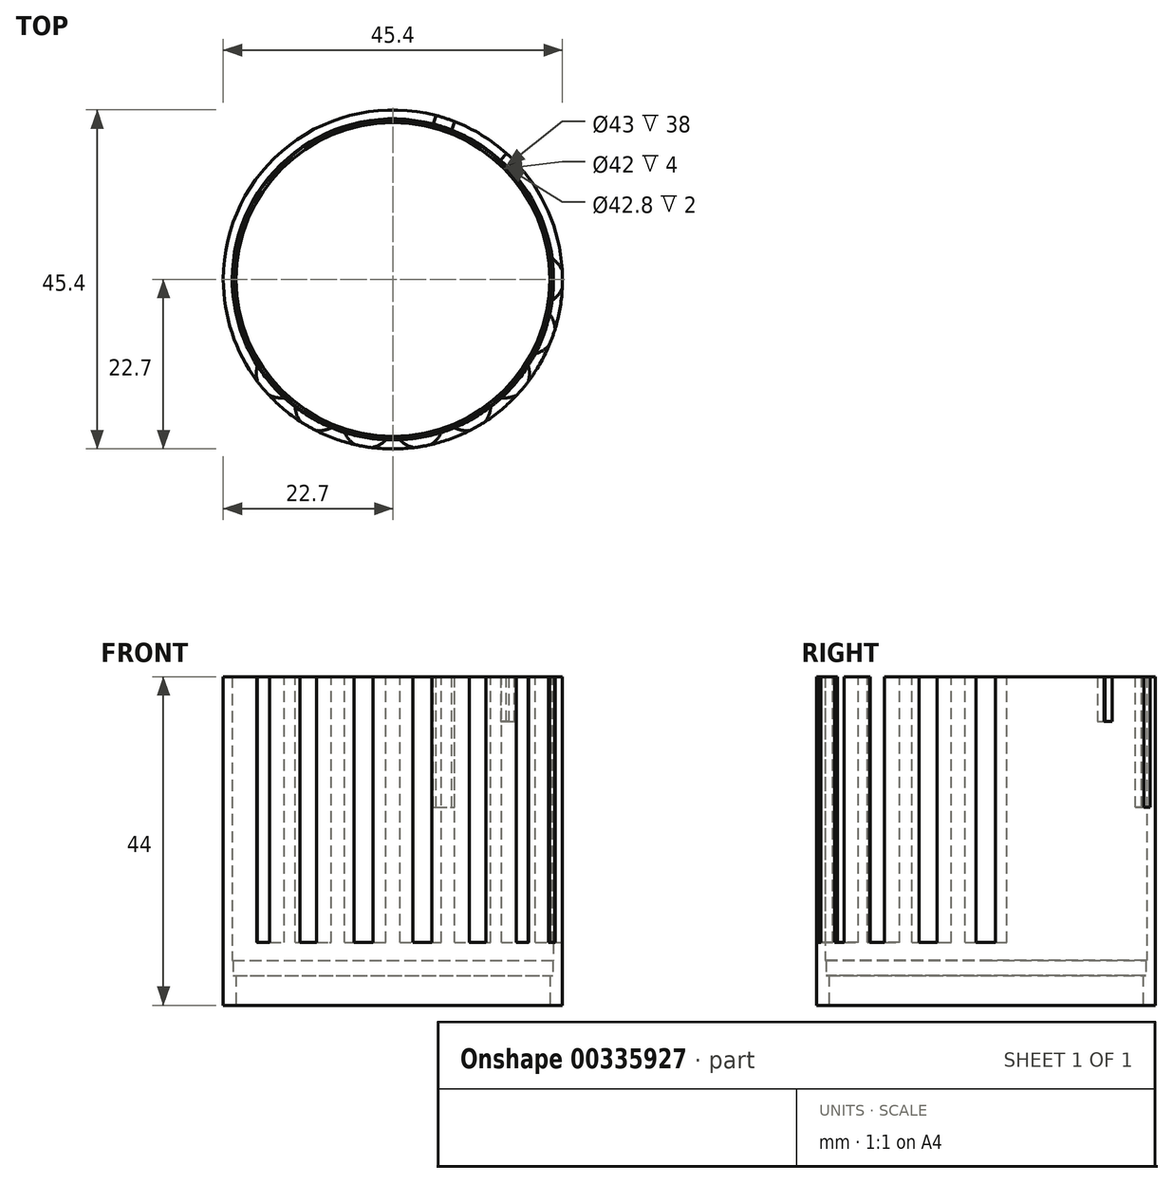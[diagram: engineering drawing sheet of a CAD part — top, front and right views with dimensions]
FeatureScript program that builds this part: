
annotation { "Feature Type Name" : "Feature", "Feature Type Description" : "" }
export const myFeature = defineFeature(function(context is Context, id is Id, definition is map)
    precondition{}
    {
        {
            var Q0;
            Q0=qCreatedBy(makeId("Front.planeOp"),FACE);
            var sketch = newSketch(context, id + "F0", { "sketchPlane" : qUnion([Q0])});
            skLineSegment(sketch, "E0", {"start": v(-22.7, 0) * mm, "end": v(-22.7, 44) * mm});
            skLineSegment(sketch, "E1", {"start": v(-22.7, 44) * mm, "end": v(-21.5, 44) * mm});
            skLineSegment(sketch, "E2", {"start": v(-21.5, 44) * mm, "end": v(-21.5, 6) * mm});
            skLineSegment(sketch, "E3", {"start": v(-21.5, 6) * mm, "end": v(-21.4, 6) * mm});
            skLineSegment(sketch, "E4", {"start": v(-21.4, 6) * mm, "end": v(-21.4, 4) * mm});
            skLineSegment(sketch, "E5", {"start": v(-21.4, 4) * mm, "end": v(-21, 4) * mm});
            skLineSegment(sketch, "E6", {"start": v(-21, 4) * mm, "end": v(-21, 0) * mm});
            skLineSegment(sketch, "E7", {"start": v(-21, 0) * mm, "end": v(-22.7, 0) * mm});
            skLineSegment(sketch, "E8", {"start": v(0, 0) * mm, "end": v(0, 44) * mm, "construction": true});
            skSolve(sketch);
        }
        {
            var Q0;
            Q0 = qSketchRegion(id + "F0", true);
            var Q1;
            Q1=sQuery(id+"F0.wireOp",EDGE,"E8");
            revolve(context, id + "F1", {"entities" : qUnion([Q0]), "axis" : qUnion([Q1]), "revolveType" : RevolveType.FULL});
        }
        {
            var Q0;
            Q0=makeQuery(id+"F1.opRevolve","SWEPT_FACE",FACE,{"disambiguationData":[OSD([sQuery(id+"F0.wireOp",EDGE,"E1")])]});
            var sketch = newSketch(context, id + "F2", { "sketchPlane" : qUnion([Q0])});
            skCircle(sketch, "E9", {"center": v(0, 0) * mm, "radius": 19.57 * mm, "construction": true});
            skLineSegment(sketch, "E10", {"start": v(0, 0) * mm, "end": v(6.05, 18.6) * mm, "construction": true});
            skLineSegment(sketch, "E11", {"start": v(12.58, 14.99) * mm, "end": v(0, 0) * mm, "construction": true});
            skLineSegment(sketch, "E12", {"start": v(19.57, 0) * mm, "end": v(0, 0) * mm, "construction": true});
            skLineSegment(sketch, "E13", {"start": v(18.39, -6.7) * mm, "end": v(0, 0) * mm, "construction": true});
            skLineSegment(sketch, "E14", {"start": v(14.99, -12.58) * mm, "end": v(0, 0) * mm, "construction": true});
            skLineSegment(sketch, "E15", {"start": v(9.78, -16.95) * mm, "end": v(0, 0) * mm, "construction": true});
            skLineSegment(sketch, "E16", {"start": v(3.4, -19.27) * mm, "end": v(0, 0) * mm, "construction": true});
            skLineSegment(sketch, "E17", {"start": v(-3.4, -19.27) * mm, "end": v(0, 0) * mm, "construction": true});
            skLineSegment(sketch, "E18", {"start": v(-9.78, -16.95) * mm, "end": v(0, 0) * mm, "construction": true});
            skCircle(sketch, "E19", {"center": v(19.57, 0) * mm, "radius": 3.3 * mm});
            skCircle(sketch, "E20", {"center": v(18.39, -6.7) * mm, "radius": 3.3 * mm});
            skCircle(sketch, "E21", {"center": v(14.99, -12.58) * mm, "radius": 3.3 * mm});
            skCircle(sketch, "E22", {"center": v(9.78, -16.95) * mm, "radius": 3.3 * mm});
            skCircle(sketch, "E23", {"center": v(3.4, -19.27) * mm, "radius": 3.3 * mm});
            skCircle(sketch, "E24", {"center": v(-3.4, -19.27) * mm, "radius": 3.3 * mm});
            skCircle(sketch, "E25", {"center": v(-9.78, -16.95) * mm, "radius": 3.3 * mm});
            skLineSegment(sketch, "E26", {"start": v(0, 0) * mm, "end": v(-14.99, -12.58) * mm, "construction": true});
            skCircle(sketch, "E27", {"center": v(-14.99, -12.58) * mm, "radius": 3.3 * mm});
            skCircle(sketch, "E28.0", {"center": v(0, 0) * mm, "radius": 21 * mm, "construction": true});
            skCircle(sketch, "E29.0", {"center": v(0, 0) * mm, "radius": 22.7 * mm, "construction": true});
            skLineSegment(sketch, "E30", {"start": v(20.96, 1.3) * mm, "end": v(22.66, 1.3) * mm});
            skLineSegment(sketch, "E31.MirrorCS", {"start": v(20.96, -1.3) * mm, "end": v(22.66, -1.3) * mm});
            skLineSegment(sketch, "E32", {"start": v(20.14, -5.95) * mm, "end": v(21.74, -6.53) * mm});
            skLineSegment(sketch, "E33.MirrorCS", {"start": v(19.25, -8.4) * mm, "end": v(20.85, -8.97) * mm});
            skLineSegment(sketch, "E34", {"start": v(15.8, -11.55) * mm, "end": v(18.2, -13.57) * mm});
            skLineSegment(sketch, "E35.MirrorCS", {"start": v(14.12, -13.55) * mm, "end": v(16.53, -15.56) * mm});
            skLineSegment(sketch, "E36", {"start": v(11.6, -17.5) * mm, "end": v(12.46, -18.98) * mm});
            skLineSegment(sketch, "E37.MirrorCS", {"start": v(9.35, -18.8) * mm, "end": v(10.2, -20.28) * mm});
            skLineSegment(sketch, "E38", {"start": v(4.92, -20.42) * mm, "end": v(5.22, -22.1) * mm});
            skLineSegment(sketch, "E39", {"start": v(-2.36, -20.87) * mm, "end": v(-2.66, -22.54) * mm});
            skLineSegment(sketch, "E40", {"start": v(-9.35, -18.8) * mm, "end": v(-10.2, -20.28) * mm});
            skLineSegment(sketch, "E41", {"start": v(-15.22, -14.47) * mm, "end": v(-16.53, -15.56) * mm});
            skLineSegment(sketch, "E42.MirrorCS", {"start": v(2.36, -20.87) * mm, "end": v(2.66, -22.54) * mm});
            skLineSegment(sketch, "E43.MirrorCS", {"start": v(-4.92, -20.42) * mm, "end": v(-5.22, -22.1) * mm});
            skLineSegment(sketch, "E44.MirrorCS", {"start": v(-11.6, -17.5) * mm, "end": v(-12.46, -18.98) * mm});
            skLineSegment(sketch, "E45.MirrorCS", {"start": v(-16.9, -12.48) * mm, "end": v(-18.2, -13.57) * mm});
            skLineSegment(sketch, "E46", {"start": v(5.24, 20.34) * mm, "end": v(5.77, 21.96) * mm});
            skLineSegment(sketch, "E47.MirrorCS", {"start": v(7.71, 19.53) * mm, "end": v(8.24, 21.15) * mm});
            skArc(sketch, "E48", {"start": v(5.24, 20.34) * mm, "mid": v(6.49, 19.97) * mm, "end": v(7.71, 19.53) * mm});
            skArc(sketch, "E49", {"start": v(5.77, 21.96) * mm, "mid": v(7.01, 21.59) * mm, "end": v(8.24, 21.15) * mm});
            skLineSegment(sketch, "E50", {"start": v(14.1, 15.56) * mm, "end": v(15.2, 16.86) * mm});
            skLineSegment(sketch, "E51", {"start": v(15.18, 14.51) * mm, "end": v(16.28, 15.82) * mm});
            skArc(sketch, "E52", {"start": v(15.18, 14.51) * mm, "mid": v(14.65, 15.05) * mm, "end": v(14.1, 15.56) * mm});
            skArc(sketch, "E53", {"start": v(16.28, 15.82) * mm, "mid": v(15.75, 16.35) * mm, "end": v(15.2, 16.86) * mm});
            skSolve(sketch);
        }
        {
            var Q0;
            {var subQ0=sQuery(id+"F2.wireOp",EDGE,"E30");var subQ1=sQuery(id+"F2.wireOp",EDGE,"E19");var subQ2=makeQuery(id+"F2.imprint","INTERSECT",VERTEX,{"derivedFrom":[subQ1,subQ0]});Q0=makeQuery(id+"F2.imprint","IMPRINT",FACE,{"disambiguationData":[TD([[makeQuery(id+"F2.imprint","IMPRINT",EDGE,{"disambiguationData":[TD([[subQ2,1.0]])],"derivedFrom":subQ1}),1.0]])]});}
            var Q1;
            {var subQ0=sQuery(id+"F2.wireOp",EDGE,"E30");var subQ1=sQuery(id+"F2.wireOp",EDGE,"E19");var subQ2=makeQuery(id+"F2.imprint","INTERSECT",VERTEX,{"derivedFrom":[subQ1,subQ0]});Q1=makeQuery(id+"F2.imprint","IMPRINT",FACE,{"disambiguationData":[TD([[makeQuery(id+"F2.imprint","IMPRINT",EDGE,{"disambiguationData":[TD([[subQ2,-1.0]])],"derivedFrom":subQ1}),1.0]])]});}
            var Q2;
            {var subQ0=sQuery(id+"F2.wireOp",EDGE,"E30");var subQ1=sQuery(id+"F2.wireOp",EDGE,"E19");var subQ2=makeQuery(id+"F2.imprint","INTERSECT",VERTEX,{"derivedFrom":[subQ1,subQ0]});Q2=makeQuery(id+"F2.imprint","IMPRINT",FACE,{"disambiguationData":[TD([[makeQuery(id+"F2.imprint","IMPRINT",EDGE,{"disambiguationData":[TD([[subQ2,1.0]])],"derivedFrom":subQ1}),-1.0]])]});}
            var Q3;
            {var subQ0=sQuery(id+"F2.wireOp",EDGE,"E31.MirrorCS");var subQ1=sQuery(id+"F2.wireOp",EDGE,"E19");var subQ2=makeQuery(id+"F2.imprint","INTERSECT",VERTEX,{"derivedFrom":[subQ1,subQ0]});Q3=makeQuery(id+"F2.imprint","IMPRINT",FACE,{"disambiguationData":[TD([[makeQuery(id+"F2.imprint","IMPRINT",EDGE,{"disambiguationData":[TD([[subQ2,-1.0]])],"derivedFrom":subQ1}),-1.0]])]});}
            var Q4;
            {var subQ0=sQuery(id+"F2.wireOp",EDGE,"E31.MirrorCS");var subQ1=sQuery(id+"F2.wireOp",EDGE,"E19");var subQ2=makeQuery(id+"F2.imprint","INTERSECT",VERTEX,{"derivedFrom":[subQ1,subQ0]});Q4=makeQuery(id+"F2.imprint","IMPRINT",FACE,{"disambiguationData":[TD([[makeQuery(id+"F2.imprint","IMPRINT",EDGE,{"disambiguationData":[TD([[subQ2,1.0]])],"derivedFrom":subQ1}),1.0]])]});}
            var Q5;
            {var subQ0=sQuery(id+"F2.wireOp",EDGE,"E19");var subQ1=makeQuery(id+"F1.opRevolve","SWEPT_EDGE",EDGE,{"disambiguationData":[OSD([sQuery(id+"F0.wireOp",EDGE,"E1"),sQuery(id+"F0.wireOp",EDGE,"E2")])]});var subQ2=makeQuery(id+"F2.imprint","INTERSECT",VERTEX,{"disambiguationData":[OD(0.0)],"derivedFrom":[subQ1,subQ0]});Q5=makeQuery(id+"F2.imprint","IMPRINT",FACE,{"disambiguationData":[TD([[makeQuery(id+"F2.imprint","IMPRINT",EDGE,{"disambiguationData":[TD([[subQ2,-1.0]])],"derivedFrom":subQ0}),1.0]])]});}
            var Q6;
            {var subQ0=sQuery(id+"F2.wireOp",EDGE,"E20");var subQ1=makeQuery(id+"F1.opRevolve","SWEPT_EDGE",EDGE,{"disambiguationData":[OSD([sQuery(id+"F0.wireOp",EDGE,"E1"),sQuery(id+"F0.wireOp",EDGE,"E2")])]});var subQ2=makeQuery(id+"F2.imprint","INTERSECT",VERTEX,{"disambiguationData":[OD(0.0)],"derivedFrom":[subQ1,subQ0]});Q6=makeQuery(id+"F2.imprint","IMPRINT",FACE,{"disambiguationData":[TD([[makeQuery(id+"F2.imprint","IMPRINT",EDGE,{"disambiguationData":[TD([[subQ2,-1.0]])],"derivedFrom":subQ0}),1.0]])]});}
            var Q7;
            {var subQ0=sQuery(id+"F2.wireOp",EDGE,"E32");var subQ1=sQuery(id+"F2.wireOp",EDGE,"E20");var subQ2=makeQuery(id+"F2.imprint","INTERSECT",VERTEX,{"derivedFrom":[subQ1,subQ0]});Q7=makeQuery(id+"F2.imprint","IMPRINT",FACE,{"disambiguationData":[TD([[makeQuery(id+"F2.imprint","IMPRINT",EDGE,{"disambiguationData":[TD([[subQ2,-1.0]])],"derivedFrom":subQ1}),1.0]])]});}
            var Q8;
            {var subQ1=sQuery(id+"F2.wireOp",EDGE,"E20");var subQ8=sQuery(id+"F2.wireOp",EDGE,"E33.MirrorCS");var subQ9=makeQuery(id+"F2.imprint","INTERSECT",VERTEX,{"derivedFrom":[subQ1,subQ8]});Q8=makeQuery(id+"F2.imprint","IMPRINT",FACE,{"disambiguationData":[TD([[makeQuery(id+"F2.imprint","IMPRINT",EDGE,{"disambiguationData":[TD([[subQ9,-1.0]])],"derivedFrom":subQ1}),1.0]])]});}
            var Q9;
            {var subQ0=sQuery(id+"F2.wireOp",EDGE,"E33.MirrorCS");var subQ1=sQuery(id+"F2.wireOp",EDGE,"E20");var subQ2=makeQuery(id+"F2.imprint","INTERSECT",VERTEX,{"derivedFrom":[subQ1,subQ0]});Q9=makeQuery(id+"F2.imprint","IMPRINT",FACE,{"disambiguationData":[TD([[makeQuery(id+"F2.imprint","IMPRINT",EDGE,{"disambiguationData":[TD([[subQ2,1.0]])],"derivedFrom":subQ1}),1.0]])]});}
            var Q10;
            {var subQ0=sQuery(id+"F2.wireOp",EDGE,"E32");var subQ1=sQuery(id+"F2.wireOp",EDGE,"E20");var subQ2=makeQuery(id+"F2.imprint","INTERSECT",VERTEX,{"derivedFrom":[subQ1,subQ0]});Q10=makeQuery(id+"F2.imprint","IMPRINT",FACE,{"disambiguationData":[TD([[makeQuery(id+"F2.imprint","IMPRINT",EDGE,{"disambiguationData":[TD([[subQ2,1.0]])],"derivedFrom":subQ1}),-1.0]])]});}
            var Q11;
            {var subQ0=sQuery(id+"F2.wireOp",EDGE,"E33.MirrorCS");var subQ1=sQuery(id+"F2.wireOp",EDGE,"E20");var subQ2=makeQuery(id+"F2.imprint","INTERSECT",VERTEX,{"derivedFrom":[subQ1,subQ0]});Q11=makeQuery(id+"F2.imprint","IMPRINT",FACE,{"disambiguationData":[TD([[makeQuery(id+"F2.imprint","IMPRINT",EDGE,{"disambiguationData":[TD([[subQ2,-1.0]])],"derivedFrom":subQ1}),-1.0]])]});}
            var Q12;
            {var subQ0=sQuery(id+"F2.wireOp",EDGE,"E21");var subQ1=makeQuery(id+"F1.opRevolve","SWEPT_EDGE",EDGE,{"disambiguationData":[OSD([sQuery(id+"F0.wireOp",EDGE,"E1"),sQuery(id+"F0.wireOp",EDGE,"E2")])]});var subQ2=makeQuery(id+"F2.imprint","INTERSECT",VERTEX,{"disambiguationData":[OD(0.0)],"derivedFrom":[subQ1,subQ0]});Q12=makeQuery(id+"F2.imprint","IMPRINT",FACE,{"disambiguationData":[TD([[makeQuery(id+"F2.imprint","IMPRINT",EDGE,{"disambiguationData":[TD([[subQ2,1.0]])],"derivedFrom":subQ0}),1.0]])]});}
            var Q13;
            {var subQ0=sQuery(id+"F2.wireOp",EDGE,"E34");var subQ1=sQuery(id+"F2.wireOp",EDGE,"E21");var subQ2=makeQuery(id+"F2.imprint","INTERSECT",VERTEX,{"derivedFrom":[subQ1,subQ0]});Q13=makeQuery(id+"F2.imprint","IMPRINT",FACE,{"disambiguationData":[TD([[makeQuery(id+"F2.imprint","IMPRINT",EDGE,{"disambiguationData":[TD([[subQ2,-1.0]])],"derivedFrom":subQ1}),1.0]])]});}
            var Q14;
            {var subQ0=sQuery(id+"F2.wireOp",EDGE,"E35.MirrorCS");var subQ1=sQuery(id+"F2.wireOp",EDGE,"E21");var subQ2=makeQuery(id+"F2.imprint","INTERSECT",VERTEX,{"derivedFrom":[subQ1,subQ0]});Q14=makeQuery(id+"F2.imprint","IMPRINT",FACE,{"disambiguationData":[TD([[makeQuery(id+"F2.imprint","IMPRINT",EDGE,{"disambiguationData":[TD([[subQ2,-1.0]])],"derivedFrom":subQ1}),1.0]])]});}
            var Q15;
            {var subQ0=sQuery(id+"F2.wireOp",EDGE,"E35.MirrorCS");var subQ1=sQuery(id+"F2.wireOp",EDGE,"E21");var subQ2=makeQuery(id+"F2.imprint","INTERSECT",VERTEX,{"derivedFrom":[subQ1,subQ0]});Q15=makeQuery(id+"F2.imprint","IMPRINT",FACE,{"disambiguationData":[TD([[makeQuery(id+"F2.imprint","IMPRINT",EDGE,{"disambiguationData":[TD([[subQ2,1.0]])],"derivedFrom":subQ1}),1.0]])]});}
            var Q16;
            {var subQ0=sQuery(id+"F2.wireOp",EDGE,"E34");var subQ1=sQuery(id+"F2.wireOp",EDGE,"E21");var subQ2=makeQuery(id+"F2.imprint","INTERSECT",VERTEX,{"derivedFrom":[subQ1,subQ0]});Q16=makeQuery(id+"F2.imprint","IMPRINT",FACE,{"disambiguationData":[TD([[makeQuery(id+"F2.imprint","IMPRINT",EDGE,{"disambiguationData":[TD([[subQ2,1.0]])],"derivedFrom":subQ1}),-1.0]])]});}
            var Q17;
            {var subQ0=sQuery(id+"F2.wireOp",EDGE,"E35.MirrorCS");var subQ1=sQuery(id+"F2.wireOp",EDGE,"E21");var subQ2=makeQuery(id+"F2.imprint","INTERSECT",VERTEX,{"derivedFrom":[subQ1,subQ0]});Q17=makeQuery(id+"F2.imprint","IMPRINT",FACE,{"disambiguationData":[TD([[makeQuery(id+"F2.imprint","IMPRINT",EDGE,{"disambiguationData":[TD([[subQ2,-1.0]])],"derivedFrom":subQ1}),-1.0]])]});}
            var Q18;
            {var subQ0=sQuery(id+"F2.wireOp",EDGE,"E37.MirrorCS");var subQ1=sQuery(id+"F2.wireOp",EDGE,"E22");var subQ2=makeQuery(id+"F2.imprint","INTERSECT",VERTEX,{"derivedFrom":[subQ1,subQ0]});Q18=makeQuery(id+"F2.imprint","IMPRINT",FACE,{"disambiguationData":[TD([[makeQuery(id+"F2.imprint","IMPRINT",EDGE,{"disambiguationData":[TD([[subQ2,1.0]])],"derivedFrom":subQ1}),1.0]])]});}
            var Q19;
            {var subQ0=sQuery(id+"F2.wireOp",EDGE,"E37.MirrorCS");var subQ1=sQuery(id+"F2.wireOp",EDGE,"E22");var subQ2=makeQuery(id+"F2.imprint","INTERSECT",VERTEX,{"derivedFrom":[subQ1,subQ0]});Q19=makeQuery(id+"F2.imprint","IMPRINT",FACE,{"disambiguationData":[TD([[makeQuery(id+"F2.imprint","IMPRINT",EDGE,{"disambiguationData":[TD([[subQ2,-1.0]])],"derivedFrom":subQ1}),1.0]])]});}
            var Q20;
            {var subQ0=sQuery(id+"F2.wireOp",EDGE,"E36");var subQ1=sQuery(id+"F2.wireOp",EDGE,"E22");var subQ2=makeQuery(id+"F2.imprint","INTERSECT",VERTEX,{"derivedFrom":[subQ1,subQ0]});Q20=makeQuery(id+"F2.imprint","IMPRINT",FACE,{"disambiguationData":[TD([[makeQuery(id+"F2.imprint","IMPRINT",EDGE,{"disambiguationData":[TD([[subQ2,-1.0]])],"derivedFrom":subQ1}),1.0]])]});}
            var Q21;
            {var subQ0=sQuery(id+"F2.wireOp",EDGE,"E22");var subQ1=makeQuery(id+"F1.opRevolve","SWEPT_EDGE",EDGE,{"disambiguationData":[OSD([sQuery(id+"F0.wireOp",EDGE,"E1"),sQuery(id+"F0.wireOp",EDGE,"E2")])]});var subQ2=makeQuery(id+"F2.imprint","INTERSECT",VERTEX,{"disambiguationData":[OD(0.0)],"derivedFrom":[subQ1,subQ0]});Q21=makeQuery(id+"F2.imprint","IMPRINT",FACE,{"disambiguationData":[TD([[makeQuery(id+"F2.imprint","IMPRINT",EDGE,{"disambiguationData":[TD([[subQ2,1.0]])],"derivedFrom":subQ0}),1.0]])]});}
            var Q22;
            {var subQ0=sQuery(id+"F2.wireOp",EDGE,"E36");var subQ1=sQuery(id+"F2.wireOp",EDGE,"E22");var subQ2=makeQuery(id+"F2.imprint","INTERSECT",VERTEX,{"derivedFrom":[subQ1,subQ0]});Q22=makeQuery(id+"F2.imprint","IMPRINT",FACE,{"disambiguationData":[TD([[makeQuery(id+"F2.imprint","IMPRINT",EDGE,{"disambiguationData":[TD([[subQ2,1.0]])],"derivedFrom":subQ1}),-1.0]])]});}
            var Q23;
            {var subQ0=sQuery(id+"F2.wireOp",EDGE,"E37.MirrorCS");var subQ1=sQuery(id+"F2.wireOp",EDGE,"E22");var subQ2=makeQuery(id+"F2.imprint","INTERSECT",VERTEX,{"derivedFrom":[subQ1,subQ0]});Q23=makeQuery(id+"F2.imprint","IMPRINT",FACE,{"disambiguationData":[TD([[makeQuery(id+"F2.imprint","IMPRINT",EDGE,{"disambiguationData":[TD([[subQ2,-1.0]])],"derivedFrom":subQ1}),-1.0]])]});}
            var Q24;
            {var subQ0=sQuery(id+"F2.wireOp",EDGE,"E23");var subQ1=makeQuery(id+"F1.opRevolve","SWEPT_EDGE",EDGE,{"disambiguationData":[OSD([sQuery(id+"F0.wireOp",EDGE,"E1"),sQuery(id+"F0.wireOp",EDGE,"E2")])]});var subQ2=makeQuery(id+"F2.imprint","INTERSECT",VERTEX,{"disambiguationData":[OD(0.0)],"derivedFrom":[subQ1,subQ0]});Q24=makeQuery(id+"F2.imprint","IMPRINT",FACE,{"disambiguationData":[TD([[makeQuery(id+"F2.imprint","IMPRINT",EDGE,{"disambiguationData":[TD([[subQ2,1.0]])],"derivedFrom":subQ0}),1.0]])]});}
            var Q25;
            {var subQ0=sQuery(id+"F2.wireOp",EDGE,"E42.MirrorCS");var subQ1=sQuery(id+"F2.wireOp",EDGE,"E23");var subQ2=makeQuery(id+"F2.imprint","INTERSECT",VERTEX,{"derivedFrom":[subQ1,subQ0]});Q25=makeQuery(id+"F2.imprint","IMPRINT",FACE,{"disambiguationData":[TD([[makeQuery(id+"F2.imprint","IMPRINT",EDGE,{"disambiguationData":[TD([[subQ2,1.0]])],"derivedFrom":subQ1}),1.0]])]});}
            var Q26;
            {var subQ1=sQuery(id+"F2.wireOp",EDGE,"E23");var subQ9=sQuery(id+"F2.wireOp",EDGE,"E42.MirrorCS");var subQ10=makeQuery(id+"F2.imprint","INTERSECT",VERTEX,{"derivedFrom":[subQ1,subQ9]});Q26=makeQuery(id+"F2.imprint","IMPRINT",FACE,{"disambiguationData":[TD([[makeQuery(id+"F2.imprint","IMPRINT",EDGE,{"disambiguationData":[TD([[subQ10,-1.0]])],"derivedFrom":subQ1}),1.0]])]});}
            var Q27;
            {var subQ0=sQuery(id+"F2.wireOp",EDGE,"E38");var subQ1=sQuery(id+"F2.wireOp",EDGE,"E23");var subQ2=makeQuery(id+"F2.imprint","INTERSECT",VERTEX,{"derivedFrom":[subQ1,subQ0]});Q27=makeQuery(id+"F2.imprint","IMPRINT",FACE,{"disambiguationData":[TD([[makeQuery(id+"F2.imprint","IMPRINT",EDGE,{"disambiguationData":[TD([[subQ2,-1.0]])],"derivedFrom":subQ1}),1.0]])]});}
            var Q28;
            {var subQ0=sQuery(id+"F2.wireOp",EDGE,"E38");var subQ1=sQuery(id+"F2.wireOp",EDGE,"E23");var subQ2=makeQuery(id+"F2.imprint","INTERSECT",VERTEX,{"derivedFrom":[subQ1,subQ0]});Q28=makeQuery(id+"F2.imprint","IMPRINT",FACE,{"disambiguationData":[TD([[makeQuery(id+"F2.imprint","IMPRINT",EDGE,{"disambiguationData":[TD([[subQ2,1.0]])],"derivedFrom":subQ1}),-1.0]])]});}
            var Q29;
            {var subQ0=sQuery(id+"F2.wireOp",EDGE,"E42.MirrorCS");var subQ1=sQuery(id+"F2.wireOp",EDGE,"E23");var subQ2=makeQuery(id+"F2.imprint","INTERSECT",VERTEX,{"derivedFrom":[subQ1,subQ0]});Q29=makeQuery(id+"F2.imprint","IMPRINT",FACE,{"disambiguationData":[TD([[makeQuery(id+"F2.imprint","IMPRINT",EDGE,{"disambiguationData":[TD([[subQ2,-1.0]])],"derivedFrom":subQ1}),-1.0]])]});}
            var Q30;
            {var subQ0=sQuery(id+"F2.wireOp",EDGE,"E24");var subQ1=makeQuery(id+"F1.opRevolve","SWEPT_EDGE",EDGE,{"disambiguationData":[OSD([sQuery(id+"F0.wireOp",EDGE,"E1"),sQuery(id+"F0.wireOp",EDGE,"E2")])]});var subQ2=makeQuery(id+"F2.imprint","INTERSECT",VERTEX,{"disambiguationData":[OD(0.0)],"derivedFrom":[subQ1,subQ0]});Q30=makeQuery(id+"F2.imprint","IMPRINT",FACE,{"disambiguationData":[TD([[makeQuery(id+"F2.imprint","IMPRINT",EDGE,{"disambiguationData":[TD([[subQ2,1.0]])],"derivedFrom":subQ0}),1.0]])]});}
            var Q31;
            {var subQ0=sQuery(id+"F2.wireOp",EDGE,"E43.MirrorCS");var subQ1=sQuery(id+"F2.wireOp",EDGE,"E24");var subQ2=makeQuery(id+"F2.imprint","INTERSECT",VERTEX,{"derivedFrom":[subQ1,subQ0]});Q31=makeQuery(id+"F2.imprint","IMPRINT",FACE,{"disambiguationData":[TD([[makeQuery(id+"F2.imprint","IMPRINT",EDGE,{"disambiguationData":[TD([[subQ2,1.0]])],"derivedFrom":subQ1}),1.0]])]});}
            var Q32;
            {var subQ0=sQuery(id+"F2.wireOp",EDGE,"E43.MirrorCS");var subQ1=sQuery(id+"F2.wireOp",EDGE,"E24");var subQ2=makeQuery(id+"F2.imprint","INTERSECT",VERTEX,{"derivedFrom":[subQ1,subQ0]});Q32=makeQuery(id+"F2.imprint","IMPRINT",FACE,{"disambiguationData":[TD([[makeQuery(id+"F2.imprint","IMPRINT",EDGE,{"disambiguationData":[TD([[subQ2,-1.0]])],"derivedFrom":subQ1}),1.0]])]});}
            var Q33;
            {var subQ0=sQuery(id+"F2.wireOp",EDGE,"E39");var subQ1=sQuery(id+"F2.wireOp",EDGE,"E24");var subQ2=makeQuery(id+"F2.imprint","INTERSECT",VERTEX,{"derivedFrom":[subQ1,subQ0]});Q33=makeQuery(id+"F2.imprint","IMPRINT",FACE,{"disambiguationData":[TD([[makeQuery(id+"F2.imprint","IMPRINT",EDGE,{"disambiguationData":[TD([[subQ2,-1.0]])],"derivedFrom":subQ1}),1.0]])]});}
            var Q34;
            {var subQ0=sQuery(id+"F2.wireOp",EDGE,"E39");var subQ1=sQuery(id+"F2.wireOp",EDGE,"E24");var subQ2=makeQuery(id+"F2.imprint","INTERSECT",VERTEX,{"derivedFrom":[subQ1,subQ0]});Q34=makeQuery(id+"F2.imprint","IMPRINT",FACE,{"disambiguationData":[TD([[makeQuery(id+"F2.imprint","IMPRINT",EDGE,{"disambiguationData":[TD([[subQ2,1.0]])],"derivedFrom":subQ1}),-1.0]])]});}
            var Q35;
            {var subQ0=sQuery(id+"F2.wireOp",EDGE,"E43.MirrorCS");var subQ1=sQuery(id+"F2.wireOp",EDGE,"E24");var subQ2=makeQuery(id+"F2.imprint","INTERSECT",VERTEX,{"derivedFrom":[subQ1,subQ0]});Q35=makeQuery(id+"F2.imprint","IMPRINT",FACE,{"disambiguationData":[TD([[makeQuery(id+"F2.imprint","IMPRINT",EDGE,{"disambiguationData":[TD([[subQ2,-1.0]])],"derivedFrom":subQ1}),-1.0]])]});}
            var Q36;
            {var subQ0=sQuery(id+"F2.wireOp",EDGE,"E25");var subQ1=makeQuery(id+"F1.opRevolve","SWEPT_EDGE",EDGE,{"disambiguationData":[OSD([sQuery(id+"F0.wireOp",EDGE,"E1"),sQuery(id+"F0.wireOp",EDGE,"E2")])]});var subQ2=makeQuery(id+"F2.imprint","INTERSECT",VERTEX,{"disambiguationData":[OD(0.0)],"derivedFrom":[subQ1,subQ0]});Q36=makeQuery(id+"F2.imprint","IMPRINT",FACE,{"disambiguationData":[TD([[makeQuery(id+"F2.imprint","IMPRINT",EDGE,{"disambiguationData":[TD([[subQ2,1.0]])],"derivedFrom":subQ0}),1.0]])]});}
            var Q37;
            {var subQ0=sQuery(id+"F2.wireOp",EDGE,"E44.MirrorCS");var subQ1=sQuery(id+"F2.wireOp",EDGE,"E25");var subQ2=makeQuery(id+"F2.imprint","INTERSECT",VERTEX,{"derivedFrom":[subQ1,subQ0]});Q37=makeQuery(id+"F2.imprint","IMPRINT",FACE,{"disambiguationData":[TD([[makeQuery(id+"F2.imprint","IMPRINT",EDGE,{"disambiguationData":[TD([[subQ2,1.0]])],"derivedFrom":subQ1}),1.0]])]});}
            var Q38;
            {var subQ0=sQuery(id+"F2.wireOp",EDGE,"E44.MirrorCS");var subQ1=sQuery(id+"F2.wireOp",EDGE,"E25");var subQ2=makeQuery(id+"F2.imprint","INTERSECT",VERTEX,{"derivedFrom":[subQ1,subQ0]});Q38=makeQuery(id+"F2.imprint","IMPRINT",FACE,{"disambiguationData":[TD([[makeQuery(id+"F2.imprint","IMPRINT",EDGE,{"disambiguationData":[TD([[subQ2,-1.0]])],"derivedFrom":subQ1}),1.0]])]});}
            var Q39;
            {var subQ0=sQuery(id+"F2.wireOp",EDGE,"E40");var subQ1=sQuery(id+"F2.wireOp",EDGE,"E25");var subQ2=makeQuery(id+"F2.imprint","INTERSECT",VERTEX,{"derivedFrom":[subQ1,subQ0]});Q39=makeQuery(id+"F2.imprint","IMPRINT",FACE,{"disambiguationData":[TD([[makeQuery(id+"F2.imprint","IMPRINT",EDGE,{"disambiguationData":[TD([[subQ2,-1.0]])],"derivedFrom":subQ1}),1.0]])]});}
            var Q40;
            {var subQ0=sQuery(id+"F2.wireOp",EDGE,"E40");var subQ1=sQuery(id+"F2.wireOp",EDGE,"E25");var subQ2=makeQuery(id+"F2.imprint","INTERSECT",VERTEX,{"derivedFrom":[subQ1,subQ0]});Q40=makeQuery(id+"F2.imprint","IMPRINT",FACE,{"disambiguationData":[TD([[makeQuery(id+"F2.imprint","IMPRINT",EDGE,{"disambiguationData":[TD([[subQ2,1.0]])],"derivedFrom":subQ1}),-1.0]])]});}
            var Q41;
            {var subQ0=sQuery(id+"F2.wireOp",EDGE,"E44.MirrorCS");var subQ1=sQuery(id+"F2.wireOp",EDGE,"E25");var subQ2=makeQuery(id+"F2.imprint","INTERSECT",VERTEX,{"derivedFrom":[subQ1,subQ0]});Q41=makeQuery(id+"F2.imprint","IMPRINT",FACE,{"disambiguationData":[TD([[makeQuery(id+"F2.imprint","IMPRINT",EDGE,{"disambiguationData":[TD([[subQ2,-1.0]])],"derivedFrom":subQ1}),-1.0]])]});}
            var Q42;
            {var subQ0=sQuery(id+"F2.wireOp",EDGE,"E27");var subQ1=makeQuery(id+"F1.opRevolve","SWEPT_EDGE",EDGE,{"disambiguationData":[OSD([sQuery(id+"F0.wireOp",EDGE,"E1"),sQuery(id+"F0.wireOp",EDGE,"E2")])]});var subQ2=makeQuery(id+"F2.imprint","INTERSECT",VERTEX,{"disambiguationData":[OD(0.0)],"derivedFrom":[subQ1,subQ0]});Q42=makeQuery(id+"F2.imprint","IMPRINT",FACE,{"disambiguationData":[TD([[makeQuery(id+"F2.imprint","IMPRINT",EDGE,{"disambiguationData":[TD([[subQ2,1.0]])],"derivedFrom":subQ0}),1.0]])]});}
            var Q43;
            {var subQ0=sQuery(id+"F2.wireOp",EDGE,"E45.MirrorCS");var subQ1=sQuery(id+"F2.wireOp",EDGE,"E27");var subQ2=makeQuery(id+"F2.imprint","INTERSECT",VERTEX,{"derivedFrom":[subQ1,subQ0]});Q43=makeQuery(id+"F2.imprint","IMPRINT",FACE,{"disambiguationData":[TD([[makeQuery(id+"F2.imprint","IMPRINT",EDGE,{"disambiguationData":[TD([[subQ2,1.0]])],"derivedFrom":subQ1}),1.0]])]});}
            var Q44;
            {var subQ1=sQuery(id+"F2.wireOp",EDGE,"E27");var subQ8=sQuery(id+"F2.wireOp",EDGE,"E45.MirrorCS");var subQ9=makeQuery(id+"F2.imprint","INTERSECT",VERTEX,{"derivedFrom":[subQ1,subQ8]});Q44=makeQuery(id+"F2.imprint","IMPRINT",FACE,{"disambiguationData":[TD([[makeQuery(id+"F2.imprint","IMPRINT",EDGE,{"disambiguationData":[TD([[subQ9,-1.0]])],"derivedFrom":subQ1}),1.0]])]});}
            var Q45;
            {var subQ0=sQuery(id+"F2.wireOp",EDGE,"E41");var subQ1=sQuery(id+"F2.wireOp",EDGE,"E27");var subQ2=makeQuery(id+"F2.imprint","INTERSECT",VERTEX,{"derivedFrom":[subQ1,subQ0]});Q45=makeQuery(id+"F2.imprint","IMPRINT",FACE,{"disambiguationData":[TD([[makeQuery(id+"F2.imprint","IMPRINT",EDGE,{"disambiguationData":[TD([[subQ2,-1.0]])],"derivedFrom":subQ1}),1.0]])]});}
            var Q46;
            {var subQ0=sQuery(id+"F2.wireOp",EDGE,"E45.MirrorCS");var subQ1=sQuery(id+"F2.wireOp",EDGE,"E27");var subQ2=makeQuery(id+"F2.imprint","INTERSECT",VERTEX,{"derivedFrom":[subQ1,subQ0]});Q46=makeQuery(id+"F2.imprint","IMPRINT",FACE,{"disambiguationData":[TD([[makeQuery(id+"F2.imprint","IMPRINT",EDGE,{"disambiguationData":[TD([[subQ2,-1.0]])],"derivedFrom":subQ1}),-1.0]])]});}
            var Q47;
            {var subQ0=sQuery(id+"F2.wireOp",EDGE,"E41");var subQ1=sQuery(id+"F2.wireOp",EDGE,"E27");var subQ2=makeQuery(id+"F2.imprint","INTERSECT",VERTEX,{"derivedFrom":[subQ1,subQ0]});Q47=makeQuery(id+"F2.imprint","IMPRINT",FACE,{"disambiguationData":[TD([[makeQuery(id+"F2.imprint","IMPRINT",EDGE,{"disambiguationData":[TD([[subQ2,1.0]])],"derivedFrom":subQ1}),-1.0]])]});}
            extrude(context, id + "F3", {"entities" : qUnion([Q0, Q1, Q2, Q3, Q4, Q5, Q6, Q7, Q8, Q9, Q10, Q11, Q12, Q13, Q14, Q15, Q16, Q17, Q18, Q19, Q20, Q21, Q22, Q23, Q24, Q25, Q26, Q27, Q28, Q29, Q30, Q31, Q32, Q33, Q34, Q35, Q36, Q37, Q38, Q39, Q40, Q41, Q42, Q43, Q44, Q45, Q46, Q47]), "operationType" : NewBodyOperationType.REMOVE, "oppositeDirection" : true, "depth" : 35.6 * mm});
        }
        {
            var Q0;
            {var subQ0=sQuery(id+"F2.wireOp",EDGE,"E49");Q0=makeQuery(id+"F2.imprint","IMPRINT",FACE,{"disambiguationData":[TD([[makeQuery(id+"F2.imprint","IMPRINT",EDGE,{"derivedFrom":subQ0}),-1.0]])]});}
            var Q1;
            {var subQ0=sQuery(id+"F2.wireOp",EDGE,"E48");Q1=makeQuery(id+"F2.imprint","IMPRINT",FACE,{"disambiguationData":[TD([[makeQuery(id+"F2.imprint","IMPRINT",EDGE,{"derivedFrom":subQ0}),1.0]])]});}
            extrude(context, id + "F4", {"entities" : qUnion([Q0, Q1]), "operationType" : NewBodyOperationType.REMOVE, "oppositeDirection" : true, "depth" : 17.5 * mm});
        }
        {
            var Q0;
            {var subQ0=sQuery(id+"F2.wireOp",EDGE,"E53");Q0=makeQuery(id+"F2.imprint","IMPRINT",FACE,{"disambiguationData":[TD([[makeQuery(id+"F2.imprint","IMPRINT",EDGE,{"derivedFrom":subQ0}),-1.0]])]});}
            var Q1;
            {var subQ0=sQuery(id+"F2.wireOp",EDGE,"E52");Q1=makeQuery(id+"F2.imprint","IMPRINT",FACE,{"disambiguationData":[TD([[makeQuery(id+"F2.imprint","IMPRINT",EDGE,{"derivedFrom":subQ0}),-1.0]])]});}
            extrude(context, id + "F5", {"entities" : qUnion([Q0, Q1]), "operationType" : NewBodyOperationType.REMOVE, "oppositeDirection" : true, "depth" : 6 * mm});
        }
    });
